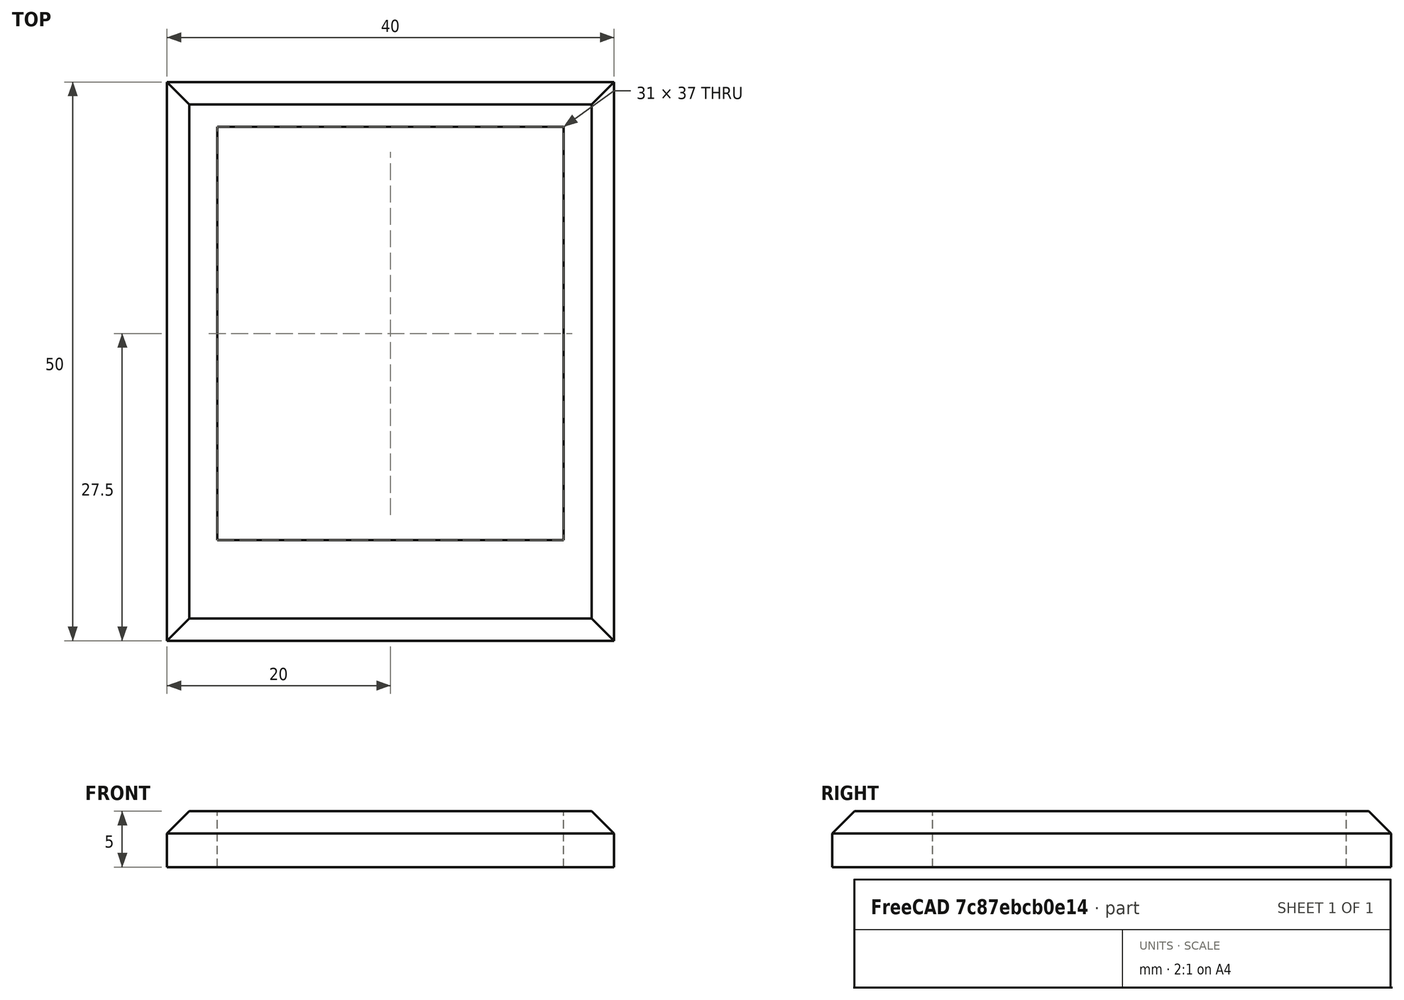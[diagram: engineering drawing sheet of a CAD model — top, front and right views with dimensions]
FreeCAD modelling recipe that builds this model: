
FCSTD DOCUMENT  (FreeCAD 0.19R24415 (Git))
Label: blende
License: All rights reserved
LicenseURL: http://en.wikipedia.org/wiki/All_rights_reserved
objects: Sketcher::SketchObject×2, PartDesign::Pad×2, PartDesign::Body×2, PartDesign::Chamfer×1, Part::Cut×1, Mesh::Feature×1
note: 11 computed .brp shape members not serialized (recipe doc carries the construction recipe); baked Part::Feature solids carry a one-line shape summary decoded from their .brp

FEATURE [Sketcher::SketchObject] Sketch
  FullyConstrained = true
  MapMode = 5
  Support = -> [XY_Plane]
  sketch-geometry (4):
    g0: LineSegment StartX=0 StartY=0 StartZ=0 EndX=40 EndY=0 EndZ=0
    g1: LineSegment StartX=40 StartY=0 StartZ=0 EndX=40 EndY=50 EndZ=0
    g2: LineSegment StartX=40 StartY=50 StartZ=0 EndX=0 EndY=50 EndZ=0
    g3: LineSegment StartX=0 StartY=50 StartZ=0 EndX=0 EndY=0 EndZ=0
  constraints (11):
    c: Coincident(g0,g1)
    c: Coincident(g1,g2)
    c: Coincident(g2,g3)
    c: Coincident(g3,g0)
    c: Horizontal(g0)
    c: Horizontal(g2)
    c: Vertical(g1)
    c: Vertical(g3)
    c: DistanceX(g2,g2) = 40
    c: DistanceY(g1,g1) = 50
    c: Coincident(g0,g-1)
FEATURE [PartDesign::Pad] Pad
  Direction = (1,1,1)
  Length = 5
  Length2 = 100
  Profile = -> Sketch
  Refine = true
  Type = 0
FEATURE [PartDesign::Chamfer] Chamfer
  Angle = 45
  Base = -> Pad [Edge10,Edge12,Edge4,Edge7]
  BaseFeature = -> Pad
  ChamferType = 0
  FlipDirection = false
  Refine = true
  Size = 2
  Size2 = 1
  SupportTransform = false
FEATURE [PartDesign::Body] Body
  Group = -> [Sketch,Pad,Chamfer]
  Origin = -> Origin
  Tip = -> Chamfer
FEATURE [Sketcher::SketchObject] Sketch001
  FullyConstrained = true
  MapMode = 5
  Support = -> [XY_Plane001]
  sketch-geometry (4):
    g0: LineSegment StartX=4.5 StartY=46 StartZ=0 EndX=35.5 EndY=46 EndZ=0
    g1: LineSegment StartX=35.5 StartY=46 StartZ=0 EndX=35.5 EndY=9 EndZ=0
    g2: LineSegment StartX=35.5 StartY=9 StartZ=0 EndX=4.5 EndY=9 EndZ=0
    g3: LineSegment StartX=4.5 StartY=9 StartZ=0 EndX=4.5 EndY=46 EndZ=0
  constraints (12):
    c: Coincident(g0,g1)
    c: Coincident(g1,g2)
    c: Coincident(g2,g3)
    c: Coincident(g3,g0)
    c: Horizontal(g0)
    c: Horizontal(g2)
    c: Vertical(g1)
    c: Vertical(g3)
    c: DistanceY(g1,g1) = 37
    c: DistanceX(g0,g0) = 31
    c: DistanceX(g-1,g0) = 4.5
    c: DistanceY(g-1,g2) = 9
FEATURE [PartDesign::Pad] Pad001
  Direction = (1,1,1)
  Length = 50
  Length2 = 100
  Profile = -> Sketch001
  Refine = true
  Type = 0
FEATURE [PartDesign::Body] Body001
  Group = -> [Sketch001,Pad001]
  Origin = -> Origin001
  Placement = pos=(0,0,-20) rot=(0,0,1;0rad)
  Tip = -> Pad001
FEATURE [Part::Cut] Cut
  Base = -> Body
  Refine = true
  Tool = -> Body001
FEATURE [Mesh::Feature] Mesh  label="Cut (Meshed)"
